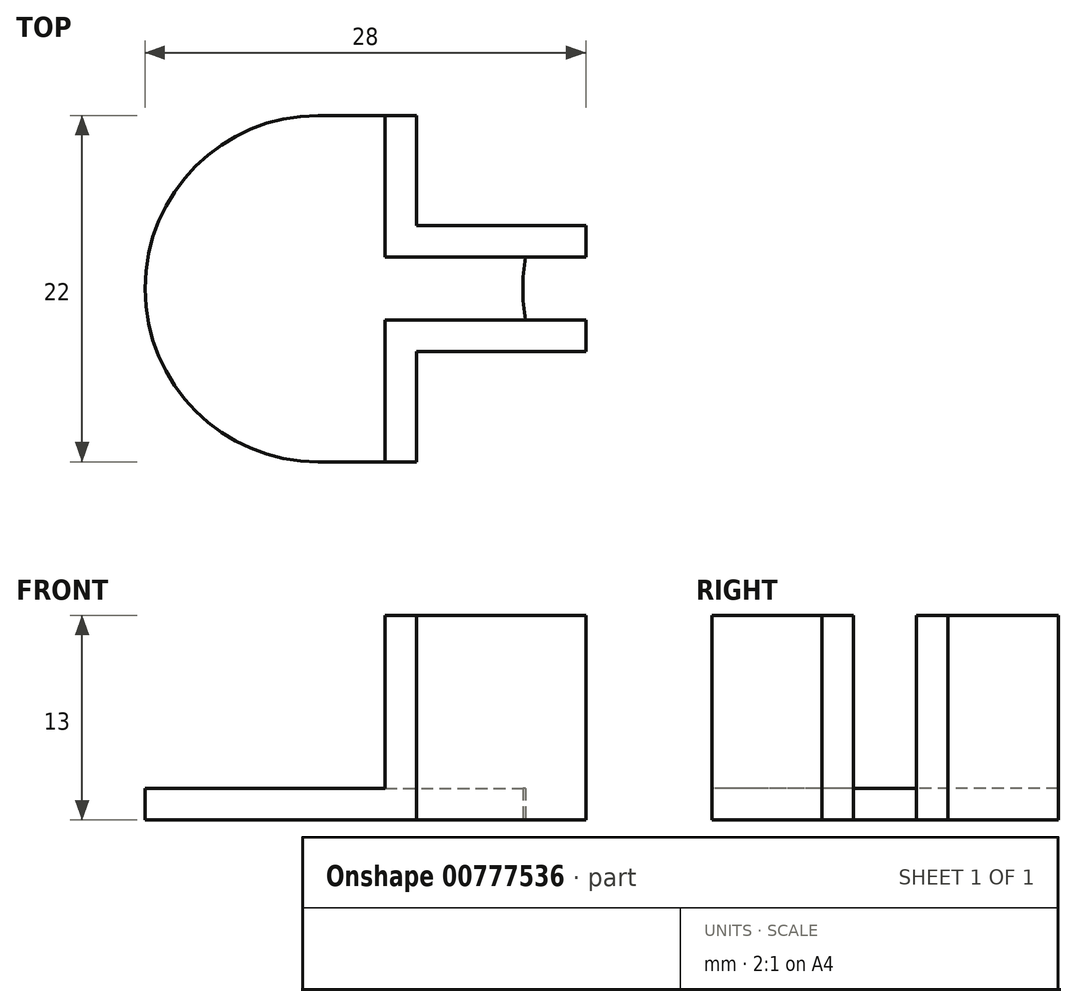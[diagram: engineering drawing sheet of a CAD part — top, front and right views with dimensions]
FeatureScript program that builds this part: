
annotation { "Feature Type Name" : "Feature", "Feature Type Description" : "" }
export const myFeature = defineFeature(function(context is Context, id is Id, definition is map)
    precondition{}
    {
        {
            var Q0;
            Q0=qCreatedBy(makeId("Top.planeOp"),FACE);
            var sketch = newSketch(context, id + "F0", { "sketchPlane" : qUnion([Q0])});
            skCircle(sketch, "E0", {"center": v(0, 0) * mm, "radius": 11 * mm});
            skCircle(sketch, "E1", {"center": v(24, 0) * mm, "radius": 11 * mm});
            skLineSegment(sketch, "E2.bottom", {"start": v(0, 11) * mm, "end": v(17, 11) * mm});
            skLineSegment(sketch, "E2.top", {"start": v(0, -11) * mm, "end": v(17, -11) * mm});
            skLineSegment(sketch, "E2.left", {"start": v(0, 11) * mm, "end": v(0, -11) * mm});
            skLineSegment(sketch, "E2.right", {"start": v(17, 11) * mm, "end": v(17, -11) * mm});
            skLineSegment(sketch, "E3.bottom", {"start": v(6.25, 4) * mm, "end": v(17, 4) * mm});
            skLineSegment(sketch, "E3.top", {"start": v(6.25, -4) * mm, "end": v(17, -4) * mm});
            skLineSegment(sketch, "E3.left", {"start": v(6.25, 4) * mm, "end": v(6.25, -4) * mm});
            skLineSegment(sketch, "E3.right", {"start": v(17, 4) * mm, "end": v(17, -4) * mm});
            skLineSegment(sketch, "E4", {"start": v(6.25, 11) * mm, "end": v(6.25, -11) * mm});
            skLineSegment(sketch, "E5", {"start": v(17, -2) * mm, "end": v(4.25, -2) * mm});
            skLineSegment(sketch, "E6", {"start": v(4.25, -11) * mm, "end": v(4.25, -2) * mm});
            skLineSegment(sketch, "E7", {"start": v(17, 2) * mm, "end": v(4.25, 2) * mm});
            skLineSegment(sketch, "E8", {"start": v(4.25, 2) * mm, "end": v(4.25, 11) * mm});
            skSolve(sketch);
        }
        {
            var Q0;
            {var subQ0=sQuery(id+"F0.wireOp",EDGE,"E2.bottom");var subQ3=sQuery(id+"F0.wireOp",EDGE,"E4");var subQ5=makeQuery(id+"F0.imprint","INTERSECT",VERTEX,{"derivedFrom":[subQ0,subQ3]});Q0=makeQuery(id+"F0.imprint","IMPRINT",FACE,{"disambiguationData":[TD([[makeQuery(id+"F0.imprint","IMPRINT",EDGE,{"disambiguationData":[TD([[subQ5,-1.0]])],"derivedFrom":subQ3}),-1.0]])]});}
            var Q1;
            {var subQ4=sQuery(id+"F0.wireOp",EDGE,"E2.left");Q1=makeQuery(id+"F0.imprint","IMPRINT",FACE,{"disambiguationData":[TD([[makeQuery(id+"F0.imprint","IMPRINT",EDGE,{"derivedFrom":subQ4}),1.0]])]});}
            var Q2;
            {var subQ0=sQuery(id+"F0.wireOp",EDGE,"E2.left");Q2=makeQuery(id+"F0.imprint","IMPRINT",FACE,{"disambiguationData":[TD([[makeQuery(id+"F0.imprint","IMPRINT",EDGE,{"derivedFrom":subQ0}),-1.0]])]});}
            var Q3;
            {var subQ0=sQuery(id+"F0.wireOp",EDGE,"E2.top");var subQ3=sQuery(id+"F0.wireOp",EDGE,"E4");var subQ5=makeQuery(id+"F0.imprint","INTERSECT",VERTEX,{"derivedFrom":[subQ0,subQ3]});Q3=makeQuery(id+"F0.imprint","IMPRINT",FACE,{"disambiguationData":[TD([[makeQuery(id+"F0.imprint","IMPRINT",EDGE,{"disambiguationData":[TD([[subQ5,1.0]])],"derivedFrom":subQ3}),-1.0]])]});}
            var Q4;
            {var subQ0=sQuery(id+"F0.wireOp",EDGE,"E3.bottom");var subQ1=sQuery(id+"F0.wireOp",EDGE,"E0");var subQ2=makeQuery(id+"F0.imprint","INTERSECT",VERTEX,{"derivedFrom":[subQ1,subQ0]});Q4=makeQuery(id+"F0.imprint","IMPRINT",FACE,{"disambiguationData":[TD([[makeQuery(id+"F0.imprint","IMPRINT",EDGE,{"disambiguationData":[TD([[subQ2,1.0]])],"derivedFrom":subQ1}),1.0]])]});}
            var Q5;
            {var subQ0=sQuery(id+"F0.wireOp",EDGE,"E3.bottom");var subQ1=sQuery(id+"F0.wireOp",EDGE,"E0");var subQ2=makeQuery(id+"F0.imprint","INTERSECT",VERTEX,{"derivedFrom":[subQ1,subQ0]});Q5=makeQuery(id+"F0.imprint","IMPRINT",FACE,{"disambiguationData":[TD([[makeQuery(id+"F0.imprint","IMPRINT",EDGE,{"disambiguationData":[TD([[subQ2,1.0]])],"derivedFrom":subQ1}),-1.0]])]});}
            var Q6;
            {var subQ5=sQuery(id+"F0.wireOp",EDGE,"E3.right");Q6=makeQuery(id+"F0.imprint","IMPRINT",FACE,{"disambiguationData":[TD([[makeQuery(id+"F0.imprint","IMPRINT",EDGE,{"derivedFrom":subQ5}),-1.0]])]});}
            var Q7;
            {var subQ0=sQuery(id+"F0.wireOp",EDGE,"E7");var subQ1=sQuery(id+"F0.wireOp",EDGE,"E0");var subQ2=makeQuery(id+"F0.imprint","INTERSECT",VERTEX,{"derivedFrom":[subQ1,subQ0]});Q7=makeQuery(id+"F0.imprint","IMPRINT",FACE,{"disambiguationData":[TD([[makeQuery(id+"F0.imprint","IMPRINT",EDGE,{"disambiguationData":[TD([[subQ2,1.0]])],"derivedFrom":subQ1}),1.0]])]});}
            var Q8;
            {var subQ0=sQuery(id+"F0.wireOp",EDGE,"E7");var subQ1=sQuery(id+"F0.wireOp",EDGE,"E0");var subQ2=makeQuery(id+"F0.imprint","INTERSECT",VERTEX,{"derivedFrom":[subQ1,subQ0]});Q8=makeQuery(id+"F0.imprint","IMPRINT",FACE,{"disambiguationData":[TD([[makeQuery(id+"F0.imprint","IMPRINT",EDGE,{"disambiguationData":[TD([[subQ2,1.0]])],"derivedFrom":subQ1}),-1.0]])]});}
            var Q9;
            {var subQ4=sQuery(id+"F0.wireOp",EDGE,"E6");var subQ6=sQuery(id+"F0.wireOp",EDGE,"E0");var subQ8=makeQuery(id+"F0.imprint","INTERSECT",VERTEX,{"derivedFrom":[subQ6,subQ4]});Q9=makeQuery(id+"F0.imprint","IMPRINT",FACE,{"disambiguationData":[TD([[makeQuery(id+"F0.imprint","IMPRINT",EDGE,{"disambiguationData":[TD([[subQ8,-1.0]])],"derivedFrom":subQ6}),1.0]])]});}
            var Q10;
            {var subQ0=sQuery(id+"F0.wireOp",EDGE,"E3.top");var subQ1=sQuery(id+"F0.wireOp",EDGE,"E0");var subQ2=makeQuery(id+"F0.imprint","INTERSECT",VERTEX,{"derivedFrom":[subQ1,subQ0]});Q10=makeQuery(id+"F0.imprint","IMPRINT",FACE,{"disambiguationData":[TD([[makeQuery(id+"F0.imprint","IMPRINT",EDGE,{"disambiguationData":[TD([[subQ2,-1.0]])],"derivedFrom":subQ1}),1.0]])]});}
            var Q11;
            {var subQ0=sQuery(id+"F0.wireOp",EDGE,"E3.top");var subQ1=sQuery(id+"F0.wireOp",EDGE,"E0");var subQ2=makeQuery(id+"F0.imprint","INTERSECT",VERTEX,{"derivedFrom":[subQ1,subQ0]});Q11=makeQuery(id+"F0.imprint","IMPRINT",FACE,{"disambiguationData":[TD([[makeQuery(id+"F0.imprint","IMPRINT",EDGE,{"disambiguationData":[TD([[subQ2,-1.0]])],"derivedFrom":subQ1}),-1.0]])]});}
            var Q12;
            {var subQ0=sQuery(id+"F0.wireOp",EDGE,"E4");var subQ6=sQuery(id+"F0.wireOp",EDGE,"E0");var subQ7=makeQuery(id+"F0.imprint","INTERSECT",VERTEX,{"disambiguationData":[OD(0.0)],"derivedFrom":[subQ6,subQ0]});Q12=makeQuery(id+"F0.imprint","IMPRINT",FACE,{"disambiguationData":[TD([[makeQuery(id+"F0.imprint","IMPRINT",EDGE,{"disambiguationData":[TD([[subQ7,-1.0]])],"derivedFrom":subQ6}),1.0]])]});}
            var Q13;
            {var subQ0=sQuery(id+"F0.wireOp",EDGE,"E2.top");var subQ3=sQuery(id+"F0.wireOp",EDGE,"E6");var subQ5=makeQuery(id+"F0.imprint","INTERSECT",VERTEX,{"derivedFrom":[subQ0,subQ3]});Q13=makeQuery(id+"F0.imprint","IMPRINT",FACE,{"disambiguationData":[TD([[makeQuery(id+"F0.imprint","IMPRINT",EDGE,{"disambiguationData":[TD([[subQ5,-1.0]])],"derivedFrom":subQ3}),1.0]])]});}
            var Q14;
            {var subQ0=sQuery(id+"F0.wireOp",EDGE,"E2.bottom");var subQ3=sQuery(id+"F0.wireOp",EDGE,"E8");var subQ5=makeQuery(id+"F0.imprint","INTERSECT",VERTEX,{"derivedFrom":[subQ0,subQ3]});Q14=makeQuery(id+"F0.imprint","IMPRINT",FACE,{"disambiguationData":[TD([[makeQuery(id+"F0.imprint","IMPRINT",EDGE,{"disambiguationData":[TD([[subQ5,1.0]])],"derivedFrom":subQ3}),1.0]])]});}
            extrude(context, id + "F1", {"entities" : qUnion([Q0, Q1, Q2, Q3, Q4, Q5, Q6, Q7, Q8, Q9, Q10, Q11, Q12, Q13, Q14]), "depth" : 2 * mm, "offsetDistance" : 25 * mm});
        }
        {
            var Q0;
            {var subQ0=sQuery(id+"F0.wireOp",EDGE,"E4");var subQ6=sQuery(id+"F0.wireOp",EDGE,"E0");var subQ7=makeQuery(id+"F0.imprint","INTERSECT",VERTEX,{"disambiguationData":[OD(0.0)],"derivedFrom":[subQ6,subQ0]});Q0=makeQuery(id+"F0.imprint","IMPRINT",FACE,{"disambiguationData":[TD([[makeQuery(id+"F0.imprint","IMPRINT",EDGE,{"disambiguationData":[TD([[subQ7,-1.0]])],"derivedFrom":subQ6}),1.0]])]});}
            var Q1;
            {var subQ0=sQuery(id+"F0.wireOp",EDGE,"E4");var subQ1=sQuery(id+"F0.wireOp",EDGE,"E0");var subQ2=makeQuery(id+"F0.imprint","INTERSECT",VERTEX,{"disambiguationData":[OD(0.0)],"derivedFrom":[subQ1,subQ0]});Q1=makeQuery(id+"F0.imprint","IMPRINT",FACE,{"disambiguationData":[TD([[makeQuery(id+"F0.imprint","IMPRINT",EDGE,{"disambiguationData":[TD([[subQ2,-1.0]])],"derivedFrom":subQ1}),-1.0]])]});}
            var Q2;
            {var subQ0=sQuery(id+"F0.wireOp",EDGE,"E3.bottom");var subQ1=sQuery(id+"F0.wireOp",EDGE,"E0");var subQ2=makeQuery(id+"F0.imprint","INTERSECT",VERTEX,{"derivedFrom":[subQ1,subQ0]});Q2=makeQuery(id+"F0.imprint","IMPRINT",FACE,{"disambiguationData":[TD([[makeQuery(id+"F0.imprint","IMPRINT",EDGE,{"disambiguationData":[TD([[subQ2,1.0]])],"derivedFrom":subQ1}),1.0]])]});}
            var Q3;
            {var subQ0=sQuery(id+"F0.wireOp",EDGE,"E3.bottom");var subQ1=sQuery(id+"F0.wireOp",EDGE,"E0");var subQ2=makeQuery(id+"F0.imprint","INTERSECT",VERTEX,{"derivedFrom":[subQ1,subQ0]});Q3=makeQuery(id+"F0.imprint","IMPRINT",FACE,{"disambiguationData":[TD([[makeQuery(id+"F0.imprint","IMPRINT",EDGE,{"disambiguationData":[TD([[subQ2,1.0]])],"derivedFrom":subQ1}),-1.0]])]});}
            var Q4;
            {var subQ0=sQuery(id+"F0.wireOp",EDGE,"E3.bottom");var subQ1=sQuery(id+"F0.wireOp",EDGE,"E1");var subQ2=makeQuery(id+"F0.imprint","INTERSECT",VERTEX,{"derivedFrom":[subQ1,subQ0]});Q4=makeQuery(id+"F0.imprint","IMPRINT",FACE,{"disambiguationData":[TD([[makeQuery(id+"F0.imprint","IMPRINT",EDGE,{"disambiguationData":[TD([[subQ2,-1.0]])],"derivedFrom":subQ1}),1.0]])]});}
            var Q5;
            {var subQ4=sQuery(id+"F0.wireOp",EDGE,"E6");var subQ6=sQuery(id+"F0.wireOp",EDGE,"E0");var subQ8=makeQuery(id+"F0.imprint","INTERSECT",VERTEX,{"derivedFrom":[subQ6,subQ4]});Q5=makeQuery(id+"F0.imprint","IMPRINT",FACE,{"disambiguationData":[TD([[makeQuery(id+"F0.imprint","IMPRINT",EDGE,{"disambiguationData":[TD([[subQ8,-1.0]])],"derivedFrom":subQ6}),1.0]])]});}
            var Q6;
            {var subQ0=sQuery(id+"F0.wireOp",EDGE,"E3.top");var subQ1=sQuery(id+"F0.wireOp",EDGE,"E0");var subQ2=makeQuery(id+"F0.imprint","INTERSECT",VERTEX,{"derivedFrom":[subQ1,subQ0]});Q6=makeQuery(id+"F0.imprint","IMPRINT",FACE,{"disambiguationData":[TD([[makeQuery(id+"F0.imprint","IMPRINT",EDGE,{"disambiguationData":[TD([[subQ2,-1.0]])],"derivedFrom":subQ1}),1.0]])]});}
            var Q7;
            {var subQ0=sQuery(id+"F0.wireOp",EDGE,"E3.top");var subQ1=sQuery(id+"F0.wireOp",EDGE,"E0");var subQ2=makeQuery(id+"F0.imprint","INTERSECT",VERTEX,{"derivedFrom":[subQ1,subQ0]});Q7=makeQuery(id+"F0.imprint","IMPRINT",FACE,{"disambiguationData":[TD([[makeQuery(id+"F0.imprint","IMPRINT",EDGE,{"disambiguationData":[TD([[subQ2,-1.0]])],"derivedFrom":subQ1}),-1.0]])]});}
            var Q8;
            {var subQ0=sQuery(id+"F0.wireOp",EDGE,"E5");var subQ1=sQuery(id+"F0.wireOp",EDGE,"E1");var subQ2=makeQuery(id+"F0.imprint","INTERSECT",VERTEX,{"derivedFrom":[subQ1,subQ0]});Q8=makeQuery(id+"F0.imprint","IMPRINT",FACE,{"disambiguationData":[TD([[makeQuery(id+"F0.imprint","IMPRINT",EDGE,{"disambiguationData":[TD([[subQ2,-1.0]])],"derivedFrom":subQ1}),1.0]])]});}
            var Q9;
            {var subQ0=sQuery(id+"F0.wireOp",EDGE,"E6");var subQ1=sQuery(id+"F0.wireOp",EDGE,"E0");var subQ2=makeQuery(id+"F0.imprint","INTERSECT",VERTEX,{"derivedFrom":[subQ1,subQ0]});Q9=makeQuery(id+"F0.imprint","IMPRINT",FACE,{"disambiguationData":[TD([[makeQuery(id+"F0.imprint","IMPRINT",EDGE,{"disambiguationData":[TD([[subQ2,-1.0]])],"derivedFrom":subQ1}),-1.0]])]});}
            extrude(context, id + "F2", {"entities" : qUnion([Q0, Q1, Q2, Q3, Q4, Q5, Q6, Q7, Q8, Q9]), "operationType" : NewBodyOperationType.ADD, "depth" : 13 * mm, "offsetDistance" : 25 * mm});
        }
    });
